# Revit family: PRD_FrankeWS_Snks_DisposalSink_SIRW511
name_source: partatom
category: Plumbing Fixtures
revit_build: Autodesk Revit 2018 (Build: 20190510_1515(x64)
units: mm (PartAtom-declared; Revit-internal decimal feet)

## family parameters
Cut with Voids When Loaded = Yes
Host = Face
OmniClass Number = 23.45.05.14.14.27
OmniClass Title = Service Sinks
Part Type = Normal
Room Calculation Point = No
Round Connector Dimension = Use Diameter
Shared = Yes

## types (1)
- SIRW511
    AssetType = Fixed
    BIMObjectName = PRD_AR_Sinks_DisposalSink_SIRW511
    BowlDepth = 360.00 mm
    BowlWidth = 360.00 mm
    Category = Pr_40_20_96_81, Sinks
    Color = alpine white
    Default Elevation = 925 mm  [stored 3.03478 ft]
    Description = Disposal sink for wall mounting made of MIRANIT resin-bonded mineral material. With pore-free, smooth surface (temperature-resistant up to 80°C). Alpine white colour. Round bowl with integrated circular flushing rim, internal horizontal water connection. Integral back panel with integrated brackets and holes for fixing. Fastening material included. Siphon made of plastic material DN 100 with horizontal outlet. With outlet grating made of nickel-chromium steel to prevent clogging.
    DiameterNominal = 90  [stored 0.295276 ft]
    DrainSize = 100 mm  [stored 0.328084 ft]
    DurationUnit = year
    Features = MIRANIT resin-bonded mineral material, alpine white colour. Bowl diameter 360 mm.
    Finish = Coated
    Grid = Optional
    GrossWeight = 24.50 kg
    IfcExportAs = IfcSanitaryTerminalType
    IfcExportType = SINK
    Manufacturer = KWC Group AG
    ManufacturerName = KWC Group AG
    ManufacturerURL = www.kwc.com
    Material = Mineral material
    MaterialCode = Miranit
    Model = SIRW511
    ModelNumber = 2000101200
    ModelReference = SIRW511
    Mounting = WallHung
    MountingOffset = 0 mm  [stored 0 ft]
    NBSDescription = Sinks
    NBSReference = 45-35-70/344
    Name = Disposal sink SIRW511
    NetWeight = 23.50 kg
    NominalDepth = 498 mm  [stored 1.63386 ft]
    NominalHeight = 414 mm  [stored 1.35827 ft]
    NominalWidth = 469 mm
    ProductCode = 207.0638.402
    ProductInformation = https://pim.kwc.com
    RearUpstand = No
    SinkMaterial = PRD_AR_ResinBondedMaterial_White
    SinkType = OTHER
    Size = 469 x 414 x 498 mm (W x H x D)
    Splashback = No
    Sump = No
    SumpBasket = No
    TailorMade = No
    TapLedge = No
    TypeOfMounting = Wall mounting
    URL = www.kwc.com
    Uniclass2015Code = Pr_40_20_96_81
    Uniclass2015Title = Sinks
    Uniclass2015Version = Products v1.17
    Version = 1
    WarrantyDurationUnit = year
    WasteHolePosition = Center
    WasteHoleProjection = 270.00 mm
    WasteSize = DN 100

note: [stored X ft] marks values corroborated as IEEE doubles in the binary element streams (Revit-internal decimal feet)

## geometry (parser evidence)
native form markers: Sweep x5
no freeform markers — native parametric forms only
